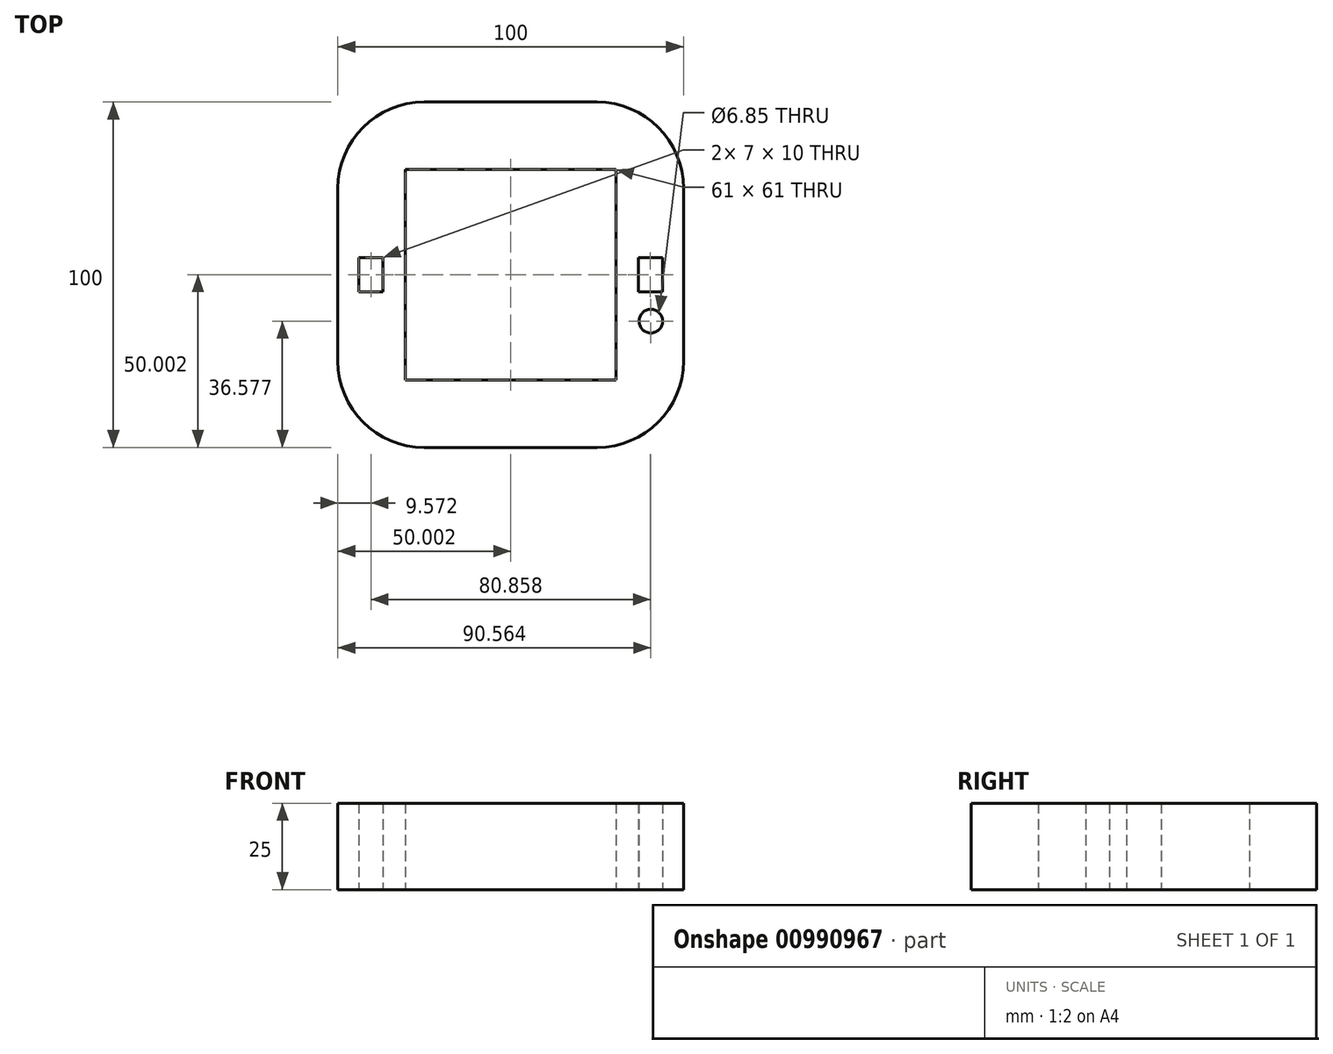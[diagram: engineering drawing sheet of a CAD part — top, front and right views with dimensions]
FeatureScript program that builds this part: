
annotation { "Feature Type Name" : "Feature", "Feature Type Description" : "" }
export const myFeature = defineFeature(function(context is Context, id is Id, definition is map)
    precondition{}
    {
        {
            var Q0;
            Q0=qCreatedBy(makeId("Top.planeOp"),FACE);
            var sketch = newSketch(context, id + "F0", { "sketchPlane" : qUnion([Q0])});
            skLineSegment(sketch, "E0.bottom", {"start": v(30.38, -30.3) * mm, "end": v(-30.62, -30.3) * mm});
            skLineSegment(sketch, "E0.top", {"start": v(30.38, 30.7) * mm, "end": v(-30.62, 30.7) * mm});
            skLineSegment(sketch, "E0.left", {"start": v(30.38, -30.3) * mm, "end": v(30.38, 30.7) * mm});
            skLineSegment(sketch, "E0.right", {"start": v(-30.62, -30.3) * mm, "end": v(-30.62, 30.7) * mm});
            skLineSegment(sketch, "E1.bottom", {"start": v(24.88, -49.8) * mm, "end": v(-25.12, -49.8) * mm});
            skLineSegment(sketch, "E1.top", {"start": v(24.88, 50.2) * mm, "end": v(-25.12, 50.2) * mm});
            skLineSegment(sketch, "E1.left", {"start": v(49.88, -24.8) * mm, "end": v(49.88, 25.2) * mm});
            skLineSegment(sketch, "E1.right", {"start": v(-50.12, -24.8) * mm, "end": v(-50.12, 25.2) * mm});
            skArc(sketch, "E2.filletArc", {"start": v(-25.12, 50.2) * mm, "mid": v(-42.8, 42.87) * mm, "end": v(-50.12, 25.2) * mm});
            skArc(sketch, "E3.filletArc", {"start": v(-50.12, -24.8) * mm, "mid": v(-42.8, -42.49) * mm, "end": v(-25.12, -49.8) * mm});
            skArc(sketch, "E4.filletArc", {"start": v(24.88, -49.8) * mm, "mid": v(42.56, -42.49) * mm, "end": v(49.88, -24.8) * mm});
            skArc(sketch, "E5.filletArc", {"start": v(49.88, 25.2) * mm, "mid": v(42.56, 42.87) * mm, "end": v(24.88, 50.2) * mm});
            skCircle(sketch, "E6", {"center": v(-40.68, -13.23) * mm, "radius": 3.43 * mm});
            skLineSegment(sketch, "E7", {"start": v(-0.12, 50.2) * mm, "end": v(-0.12, -49.8) * mm, "construction": true});
            skCircle(sketch, "E8.MirrorC", {"center": v(40.44, -13.23) * mm, "radius": 3.43 * mm});
            skLineSegment(sketch, "E9.bottom", {"start": v(-37.05, -4.8) * mm, "end": v(-44.05, -4.8) * mm});
            skLineSegment(sketch, "E9.top", {"start": v(-37.05, 5.2) * mm, "end": v(-44.05, 5.2) * mm});
            skLineSegment(sketch, "E9.left", {"start": v(-37.05, -4.8) * mm, "end": v(-37.05, 5.2) * mm});
            skLineSegment(sketch, "E9.right", {"start": v(-44.05, -4.8) * mm, "end": v(-44.05, 5.2) * mm});
            skLineSegment(sketch, "E10.MirrorCS", {"start": v(36.81, 5.2) * mm, "end": v(43.81, 5.2) * mm});
            skLineSegment(sketch, "E11.MirrorCS", {"start": v(36.81, -4.8) * mm, "end": v(36.81, 5.2) * mm});
            skLineSegment(sketch, "E12.MirrorCS", {"start": v(36.81, -4.8) * mm, "end": v(43.81, -4.8) * mm});
            skLineSegment(sketch, "E13.MirrorCS", {"start": v(43.81, -4.8) * mm, "end": v(43.81, 5.2) * mm});
            skSolve(sketch);
        }
        {
            var Q0;
            Q0=makeQuery(id+"F0.imprint","IMPRINT",FACE,{"disambiguationData":[TD([[makeQuery(id+"F0.imprint","IMPRINT",EDGE,{"derivedFrom":sQuery(id+"F0.wireOp",EDGE,"E0.bottom")}),1.0]])]});
            extrude(context, id + "F1", {"entities" : qUnion([Q0]), "depth" : 10 * mm, "offsetDistance" : 25 * mm});
        }
        {
            var Q0;
            Q0=makeQuery(id+"F0.imprint","IMPRINT",FACE,{"disambiguationData":[TD([[makeQuery(id+"F0.imprint","IMPRINT",EDGE,{"derivedFrom":sQuery(id+"F0.wireOp",EDGE,"E6")}),1.0]])]});
            var Q1;
            Q1=makeQuery(id+"F0.imprint","IMPRINT",FACE,{"disambiguationData":[TD([[makeQuery(id+"F0.imprint","IMPRINT",EDGE,{"derivedFrom":sQuery(id+"F0.wireOp",EDGE,"E8.MirrorC")}),-1.0]])]});
            extrude(context, id + "F2", {"entities" : qUnion([Q0, Q1]), "operationType" : NewBodyOperationType.ADD, "depth" : 25 * mm, "offsetDistance" : 25 * mm});
        }
    });
